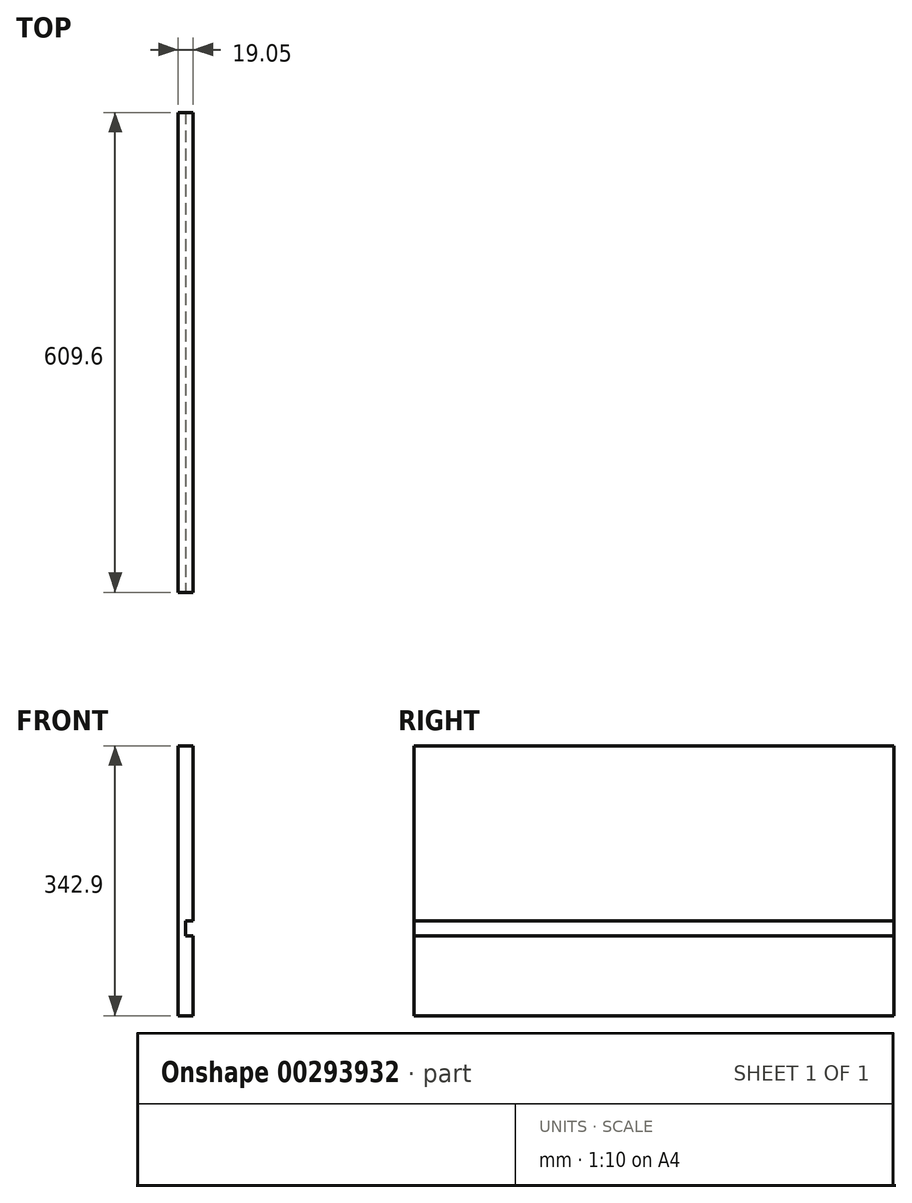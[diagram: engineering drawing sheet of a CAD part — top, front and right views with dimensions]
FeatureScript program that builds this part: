
annotation { "Feature Type Name" : "Feature", "Feature Type Description" : "" }
export const myFeature = defineFeature(function(context is Context, id is Id, definition is map)
    precondition{}
    {
        {
            var Q0;
            Q0=qCreatedBy(makeId("Front.planeOp"),FACE);
            var sketch = newSketch(context, id + "F0", { "sketchPlane" : qUnion([Q0])});
            skLineSegment(sketch, "E0.bottom", {"start": v(0, 0) * mm, "end": v(19.05, 0) * mm});
            skLineSegment(sketch, "E0.top", {"start": v(0, 342.9) * mm, "end": v(19.05, 342.9) * mm});
            skLineSegment(sketch, "E0.left", {"start": v(0, 0) * mm, "end": v(0, 342.9) * mm});
            skLineSegment(sketch, "E0.right", {"start": v(19.05, 0) * mm, "end": v(19.05, 101.6) * mm});
            skLineSegment(sketch, "E1.bottom", {"start": v(19.05, 120.65) * mm, "end": v(9.52, 120.65) * mm});
            skLineSegment(sketch, "E1.top", {"start": v(19.05, 101.6) * mm, "end": v(9.53, 101.6) * mm});
            skLineSegment(sketch, "E1.right", {"start": v(9.52, 120.65) * mm, "end": v(9.53, 101.6) * mm});
            skLineSegment(sketch, "E2.trimOffspring", {"start": v(19.05, 120.65) * mm, "end": v(19.05, 342.9) * mm});
            skSolve(sketch);
        }
        {
            var Q0;
            Q0 = qSketchRegion(id + "F0", true);
            extrude(context, id + "F1", {"entities" : qUnion([Q0]), "oppositeDirection" : true, "depth" : 609.6 * mm});
        }
    });
